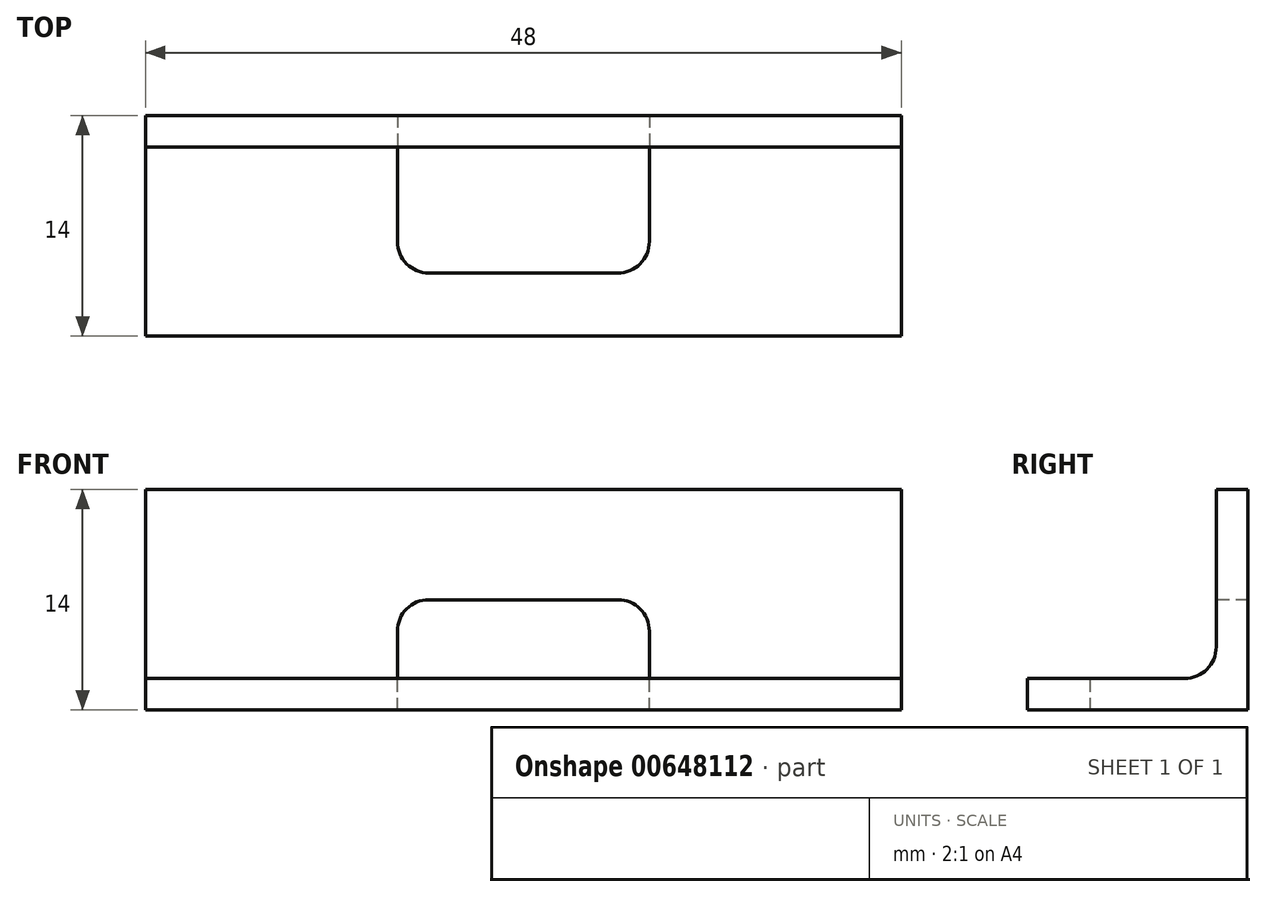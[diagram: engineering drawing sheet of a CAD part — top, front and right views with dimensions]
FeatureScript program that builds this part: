
annotation { "Feature Type Name" : "Feature", "Feature Type Description" : "" }
export const myFeature = defineFeature(function(context is Context, id is Id, definition is map)
    precondition{}
    {
        {
            var Q0;
            Q0=qCreatedBy(makeId("Right.planeOp"),FACE);
            var sketch = newSketch(context, id + "F0", { "sketchPlane" : qUnion([Q0])});
            skLineSegment(sketch, "E0.bottom", {"start": v(0, 0) * mm, "end": v(14, 0) * mm});
            skLineSegment(sketch, "E0.top", {"start": v(0, 2) * mm, "end": v(14, 2) * mm});
            skLineSegment(sketch, "E0.left", {"start": v(0, 0) * mm, "end": v(0, 2) * mm});
            skLineSegment(sketch, "E0.right", {"start": v(14, 0) * mm, "end": v(14, 2) * mm});
            skLineSegment(sketch, "E1.bottom", {"start": v(14, 2) * mm, "end": v(12, 2) * mm});
            skLineSegment(sketch, "E1.top", {"start": v(14, 14) * mm, "end": v(12, 14) * mm});
            skLineSegment(sketch, "E1.left", {"start": v(14, 2) * mm, "end": v(14, 14) * mm});
            skLineSegment(sketch, "E1.right", {"start": v(12, 2) * mm, "end": v(12, 14) * mm});
            skSolve(sketch);
        }
        {
            var Q0;
            Q0 = qSketchRegion(id + "F0", true);
            extrude(context, id + "F1", {"entities" : qUnion([Q0]), "depth" : 48 * mm, "offsetDistance" : 25 * mm});
        }
        {
            var Q0;
            Q0=makeQuery(id+"F1.opExtrude","SWEPT_FACE",FACE,{"disambiguationData":[OSD([sQuery(id+"F0.wireOp",EDGE,"E1.right")])]});
            var sketch = newSketch(context, id + "F2", { "sketchPlane" : qUnion([Q0])});
            skLineSegment(sketch, "E2.bottom", {"start": v(32, 0) * mm, "end": v(16, 0) * mm});
            skLineSegment(sketch, "E2.top", {"start": v(32, 7) * mm, "end": v(16, 7) * mm});
            skLineSegment(sketch, "E2.left", {"start": v(32, 0) * mm, "end": v(32, 7) * mm});
            skLineSegment(sketch, "E2.right", {"start": v(16, 0) * mm, "end": v(16, 7) * mm});
            skPoint(sketch, "E3", {"position": v(24, 7) * mm});
            skSolve(sketch);
        }
        {
            var Q0;
            Q0 = qSketchRegion(id + "F2", true);
            extrude(context, id + "F3", {"entities" : qUnion([Q0]), "operationType" : NewBodyOperationType.REMOVE, "endBound" : BoundingType.THROUGH_ALL, "oppositeDirection" : true, "depth" : 25 * mm, "offsetDistance" : 25 * mm, "hasSecondDirection" : true, "secondDirectionOppositeDirection" : false, "secondDirectionDepth" : 8 * mm});
        }
        {
            var Q0;
            Q0=makeQuery(id+"F3.boolean.opBoolean","COPY",EDGE,{"derivedFrom":makeQuery(id+"F3.opExtrude","CAP_EDGE",EDGE,{"disambiguationData":[OSD([sQuery(id+"F2.wireOp",EDGE,"E2.left")])],"isStart":true})});
            var Q1;
            Q1=makeQuery(id+"F3.boolean.opBoolean","COPY",EDGE,{"derivedFrom":makeQuery(id+"F3.opExtrude","CAP_EDGE",EDGE,{"disambiguationData":[OSD([sQuery(id+"F2.wireOp",EDGE,"E2.right")])],"isStart":true})});
            var Q2;
            Q2=makeQuery(id+"F3.boolean.opBoolean","COPY",EDGE,{"derivedFrom":makeQuery(id+"F3.opExtrude","SWEPT_EDGE",EDGE,{"disambiguationData":[OSD([sQuery(id+"F2.wireOp",EDGE,"E2.top"),sQuery(id+"F2.wireOp",EDGE,"E2.right")])]})});
            var Q3;
            Q3=makeQuery(id+"F3.boolean.opBoolean","COPY",EDGE,{"derivedFrom":makeQuery(id+"F3.opExtrude","SWEPT_EDGE",EDGE,{"disambiguationData":[OSD([sQuery(id+"F2.wireOp",EDGE,"E2.top"),sQuery(id+"F2.wireOp",EDGE,"E2.left")])]})});
            var Q4;
            {var subQ0=sQuery(id+"F0.wireOp",EDGE,"E1.right");var subQ1=sQuery(id+"F0.wireOp",EDGE,"E0.top");Q4=makeQuery(id+"F3.boolean.opBoolean","SPLIT",EDGE,{"disambiguationData":[TD([makeQuery(id+"F3.opExtrude","SWEPT_FACE",FACE,{"disambiguationData":[OSD([sQuery(id+"F2.wireOp",EDGE,"E2.left")])]})])],"derivedFrom":makeQuery(id+"F1.opExtrude","SWEPT_EDGE",EDGE,{"disambiguationData":[OSD([subQ1,sQuery(id+"F0.wireOp",EDGE,"E1.bottom"),subQ0])]})});}
            var Q5;
            {var subQ0=sQuery(id+"F0.wireOp",EDGE,"E1.right");var subQ1=sQuery(id+"F0.wireOp",EDGE,"E0.top");Q5=makeQuery(id+"F3.boolean.opBoolean","SPLIT",EDGE,{"disambiguationData":[TD([makeQuery(id+"F3.opExtrude","SWEPT_FACE",FACE,{"disambiguationData":[OSD([sQuery(id+"F2.wireOp",EDGE,"E2.right")])]})])],"derivedFrom":makeQuery(id+"F1.opExtrude","SWEPT_EDGE",EDGE,{"disambiguationData":[OSD([subQ1,sQuery(id+"F0.wireOp",EDGE,"E1.bottom"),subQ0])]})});}
            fillet(context, id + "F4", {"entities" : qUnion([Q0, Q1, Q2, Q3, Q4, Q5]), "radius" : 2 * mm, "tangentPropagation" : true, "allowEdgeOverflow" : false});
        }
    });
